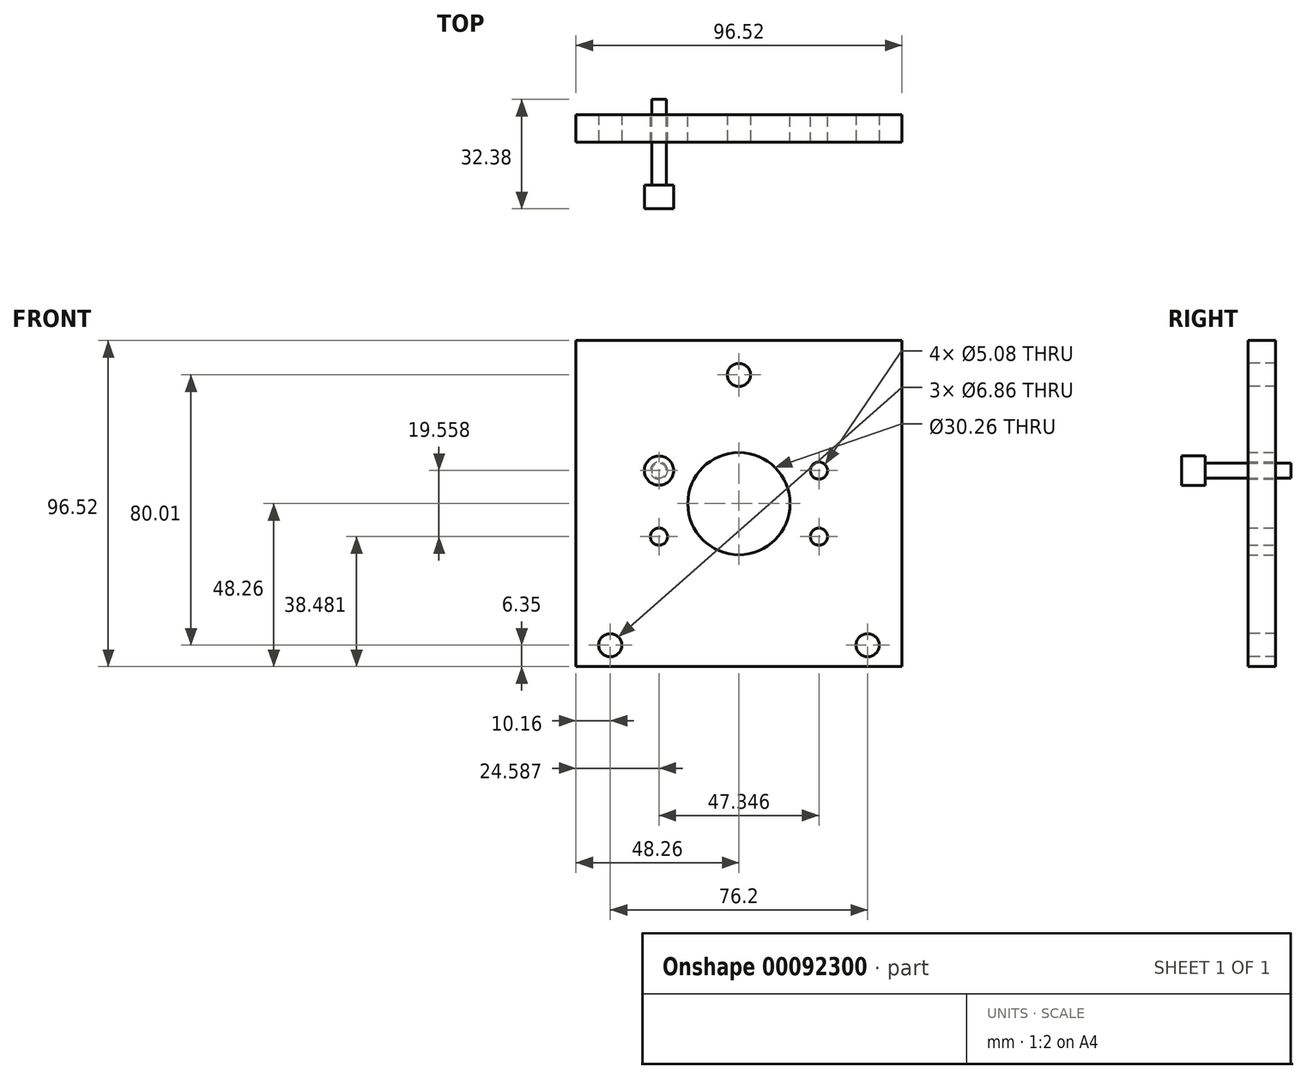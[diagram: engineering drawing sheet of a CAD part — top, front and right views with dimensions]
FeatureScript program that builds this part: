
annotation { "Feature Type Name" : "Feature", "Feature Type Description" : "" }
export const myFeature = defineFeature(function(context is Context, id is Id, definition is map)
    precondition{}
    {
        {
            var Q0;
            Q0=qCreatedBy(makeId("Front.planeOp"),FACE);
            var sketch = newSketch(context, id + "F0", { "sketchPlane" : qUnion([Q0])});
            skLineSegment(sketch, "E0.bottom", {"start": v(48.26, 48.26) * mm, "end": v(-48.26, 48.26) * mm});
            skLineSegment(sketch, "E0.top", {"start": v(48.26, -48.26) * mm, "end": v(-48.26, -48.26) * mm});
            skLineSegment(sketch, "E0.left", {"start": v(48.26, 48.26) * mm, "end": v(48.26, -48.26) * mm});
            skLineSegment(sketch, "E0.right", {"start": v(-48.26, 48.26) * mm, "end": v(-48.26, -48.26) * mm});
            skPoint(sketch, "E0.middle", {"position": v(0, 0) * mm});
            skCircle(sketch, "E1", {"center": v(0, 0) * mm, "radius": 15.13 * mm});
            skCircle(sketch, "E2", {"center": v(-23.67, 9.78) * mm, "radius": 2.54 * mm});
            skCircle(sketch, "E3", {"center": v(23.67, 9.78) * mm, "radius": 2.54 * mm});
            skCircle(sketch, "E4", {"center": v(23.67, -9.78) * mm, "radius": 2.54 * mm});
            skCircle(sketch, "E5", {"center": v(-23.67, -9.78) * mm, "radius": 2.54 * mm});
            skSolve(sketch);
        }
        {
            var Q0;
            Q0=qSketchRegion(id+"F0",true);
            extrude(context, id + "F1", {"entities" : qUnion([Q0]), "depth" : 8.18 * mm});
        }
        {
            var Q0;
            Q0=makeQuery(id+"F1.opExtrude","CAP_FACE",FACE,{"disambiguationData":[OSD([sQuery(id+"F0.wireOp",EDGE,"E0.bottom"),sQuery(id+"F0.wireOp",EDGE,"E0.top"),sQuery(id+"F0.wireOp",EDGE,"E0.left"),sQuery(id+"F0.wireOp",EDGE,"E0.right"),sQuery(id+"F0.wireOp",EDGE,"E1"),sQuery(id+"F0.wireOp",EDGE,"wpZbGDZD-WrGK-BEMo-HgKh-vHg5cBUCKiRJ"),sQuery(id+"F0.wireOp",EDGE,"YVnn6QpA-SDTv-qPej-sDvv-PzaUP0ouTEN2")])],"isStart":false});
            var sketch = newSketch(context, id + "F2", { "sketchPlane" : qUnion([Q0])});
            skCircle(sketch, "E6", {"center": v(0, 38.1) * mm, "radius": 3.43 * mm});
            skCircle(sketch, "E7", {"center": v(38.1, -41.91) * mm, "radius": 3.43 * mm});
            skCircle(sketch, "E8", {"center": v(-38.1, -41.91) * mm, "radius": 3.43 * mm});
            skSolve(sketch);
        }
        {
            var Q0;
            Q0=qSketchRegion(id+"F2",true);
            extrude(context, id + "F3", {"entities" : qUnion([Q0]), "operationType" : NewBodyOperationType.REMOVE, "endBound" : BoundingType.THROUGH_ALL, "oppositeDirection" : true, "depth" : 25.4 * mm});
        }
        {
            var Q0;
            Q0=makeQuery(id+"F1.opExtrude","CAP_FACE",FACE,{"disambiguationData":[OSD([sQuery(id+"F0.wireOp",EDGE,"E0.bottom"),sQuery(id+"F0.wireOp",EDGE,"E0.top"),sQuery(id+"F0.wireOp",EDGE,"E0.left"),sQuery(id+"F0.wireOp",EDGE,"E0.right"),sQuery(id+"F0.wireOp",EDGE,"E1"),sQuery(id+"F0.wireOp",EDGE,"E2"),sQuery(id+"F0.wireOp",EDGE,"E3"),sQuery(id+"F0.wireOp",EDGE,"E4"),sQuery(id+"F0.wireOp",EDGE,"E5")])],"isStart":false});
            var sketch = newSketch(context, id + "F4", { "sketchPlane" : qUnion([Q0])});
            skCircle(sketch, "E9", {"center": v(-23.67, 9.78) * mm, "radius": 2.19 * mm});
            skSolve(sketch);
        }
        {
            var Q0;
            Q0 = qSketchRegion(id + "F4", true);
            extrude(context, id + "F5", {"entities" : qUnion([Q0]), "endBound" : BoundingType.SYMMETRIC, "depth" : 25.4 * mm});
        }
        {
            var Q0;
            Q0=makeQuery(id+"F5.opExtrude","CAP_FACE",FACE,{"disambiguationData":[OSD([sQuery(id+"F4.wireOp",EDGE,"E9")])],"isStart":false});
            var sketch = newSketch(context, id + "F6", { "sketchPlane" : qUnion([Q0])});
            skCircle(sketch, "E10", {"center": v(-23.67, 9.78) * mm, "radius": 4.33 * mm});
            skSolve(sketch);
        }
        {
            var Q0;
            Q0 = qSketchRegion(id + "F6", true);
            extrude(context, id + "F7", {"entities" : qUnion([Q0]), "operationType" : NewBodyOperationType.ADD, "depth" : 7 * mm});
        }
    });
